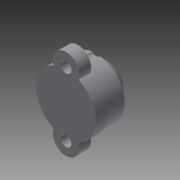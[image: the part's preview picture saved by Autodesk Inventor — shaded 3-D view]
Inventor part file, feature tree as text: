
AUTODESK INVENTOR PART (.ipt)
format: ipt  version: 2015 (Build 190159000, 159)  size: 162,304 bytes
history: native  units: mm
features: sketch x3, extrude x2, revolve x1
ambient origin geometry x8: Origin, YZ Plane, XZ Plane, XY Plane, X Axis, Y Axis, Z Axis, Center Point
bodies: Solid1 (feature_tree)
feature tree (6):
  extrude  "Extrusion1"  Depth=2.286mm
  extrude  "Extrusion2"  Depth=6.731mm
  revolve  "Revolution1"  [1 undecoded]
  sketch  "Sketch1"  dims[d0=12.7mm d1=2.286mm]
  sketch  "Sketch2"  dims[d2=2.286mm d3=6.731mm]
  sketch  "Sketch3"  dims[d4=6.731mm d5=13.462mm d6=19.05mm d7=2.54mm d8=0.0mm d9=3.81mm d10=0.0mm d11=10.16mm d12=10.16mm d13=90.0deg]
note: 1 required parameter value undecoded (feature->parameter linkage not recoverable at this tier; creation-order binding heuristic only, values carry confidence <= 0.55)
